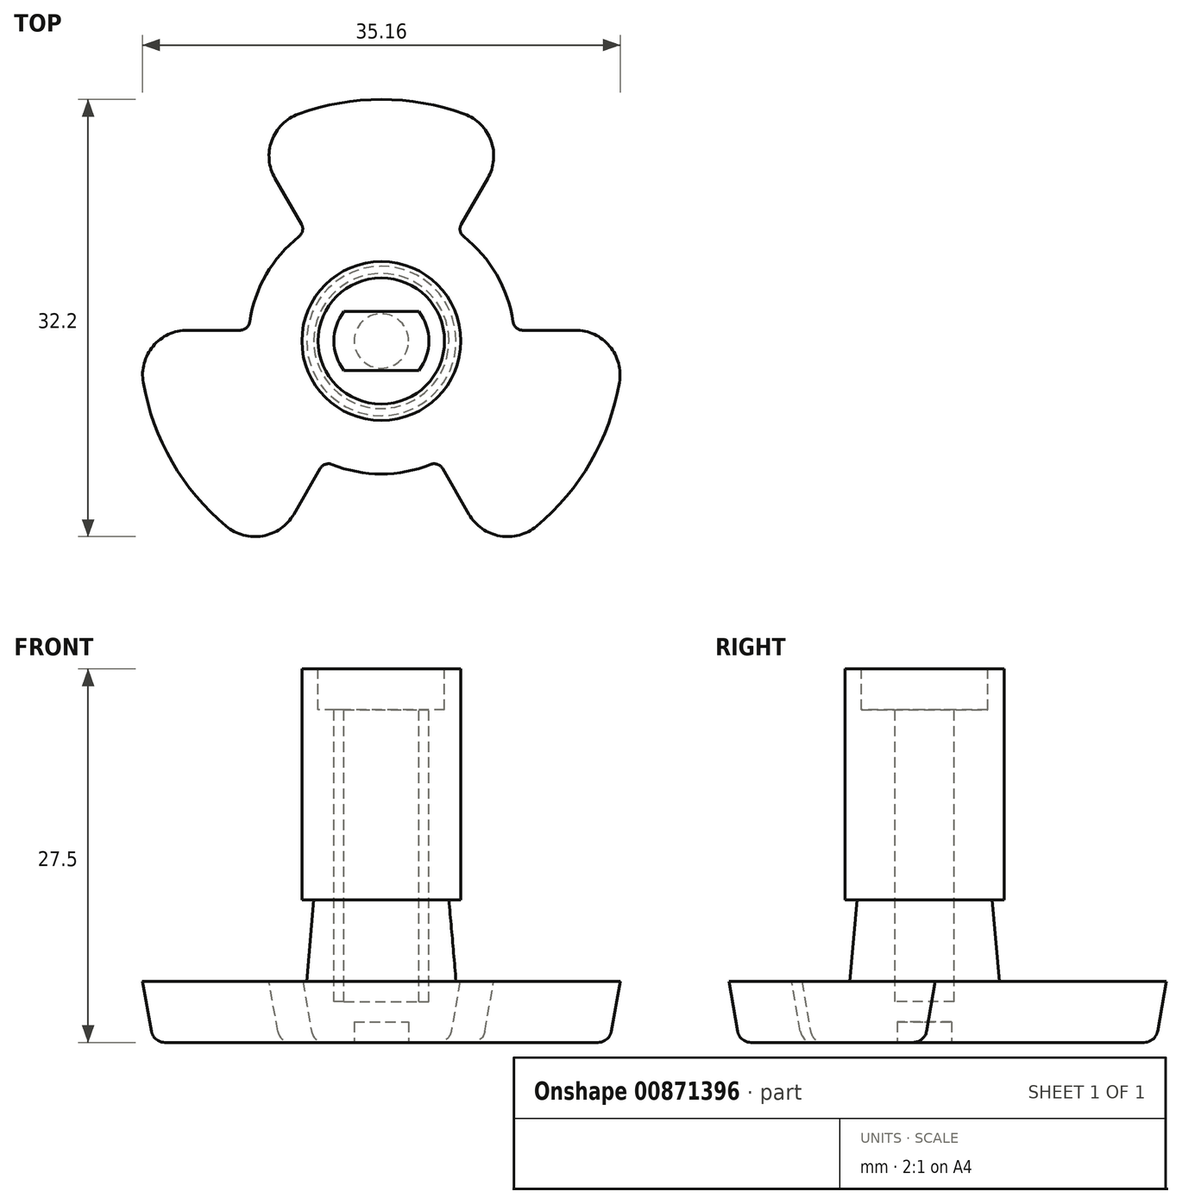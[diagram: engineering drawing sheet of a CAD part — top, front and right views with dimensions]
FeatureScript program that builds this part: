
annotation { "Feature Type Name" : "Feature", "Feature Type Description" : "" }
export const myFeature = defineFeature(function(context is Context, id is Id, definition is map)
    precondition{}
    {
        {
            var Q0;
            Q0=qCreatedBy(makeId("Top.planeOp"),FACE);
            var sketch = newSketch(context, id + "F0", { "sketchPlane" : qUnion([Q0])});
            skArc(sketch, "E0", {"start": v(-16.75, -2.93) * mm, "mid": v(-14.72, -8.5) * mm, "end": v(-10.91, -13.04) * mm});
            skLineSegment(sketch, "E1", {"start": v(-14.28, 0) * mm, "end": v(-10.4, 0) * mm});
            skLineSegment(sketch, "E2.1.0", {"start": v(7.14, -12.37) * mm, "end": v(5.2, -9) * mm});
            skLineSegment(sketch, "E2.2.0", {"start": v(7.14, 12.37) * mm, "end": v(5.2, 9) * mm});
            skArc(sketch, "E3", {"start": v(-5.57, 7.07) * mm, "mid": v(-7.8, 4.5) * mm, "end": v(-8.9, 1.29) * mm});
            skPoint(sketch, "E4.orphan", {"position": v(-10.5, 18.2) * mm});
            skPoint(sketch, "E5.orphan", {"position": v(10.95, 18.97) * mm});
            skArc(sketch, "E6.trimOffspring", {"start": v(5.83, 15.97) * mm, "mid": v(0, 17) * mm, "end": v(-5.83, 15.97) * mm});
            skPoint(sketch, "E7.orphan", {"position": v(21.02, 0) * mm});
            skArc(sketch, "E8.trimOffspring", {"start": v(10.91, -13.04) * mm, "mid": v(14.72, -8.5) * mm, "end": v(16.75, -2.93) * mm});
            skPoint(sketch, "E9.orphan", {"position": v(10.95, -18.97) * mm});
            skPoint(sketch, "E10.orphan", {"position": v(-10.5, -18.2) * mm});
            skPoint(sketch, "E11.visualSharp", {"position": v(-8.5, 14.72) * mm});
            skArc(sketch, "E11.filletArc", {"start": v(-5.83, 15.97) * mm, "mid": v(-7.33, 14.47) * mm, "end": v(-7.14, 12.37) * mm});
            skPoint(sketch, "E12.visualSharp", {"position": v(8.5, 14.72) * mm});
            skArc(sketch, "E12.filletArc", {"start": v(7.14, 12.37) * mm, "mid": v(7.33, 14.47) * mm, "end": v(5.83, 15.97) * mm});
            skPoint(sketch, "E13.visualSharp", {"position": v(17, 0) * mm});
            skArc(sketch, "E13.filletArc", {"start": v(16.75, -2.93) * mm, "mid": v(16.2, -0.9) * mm, "end": v(14.28, 0) * mm});
            skPoint(sketch, "E14.visualSharp", {"position": v(8.5, -14.72) * mm});
            skArc(sketch, "E14.filletArc", {"start": v(7.14, -12.37) * mm, "mid": v(8.87, -13.58) * mm, "end": v(10.91, -13.04) * mm});
            skPoint(sketch, "E15.visualSharp", {"position": v(-8.5, -14.72) * mm});
            skArc(sketch, "E15.filletArc", {"start": v(-10.91, -13.04) * mm, "mid": v(-8.87, -13.58) * mm, "end": v(-7.14, -12.37) * mm});
            skPoint(sketch, "E16.orphan", {"position": v(-21.9, 0) * mm});
            skPoint(sketch, "E17.visualSharp", {"position": v(-17, 0) * mm});
            skArc(sketch, "E17.filletArc", {"start": v(-14.28, 0) * mm, "mid": v(-16.2, -0.9) * mm, "end": v(-16.75, -2.93) * mm});
            skLineSegment(sketch, "E18.trimOffspring", {"start": v(-5.2, 9) * mm, "end": v(-7.14, 12.37) * mm});
            skLineSegment(sketch, "E19.trimOffspring", {"start": v(10.4, 0) * mm, "end": v(14.28, 0) * mm});
            skArc(sketch, "E20.trimOffspring", {"start": v(-3.34, -8.36) * mm, "mid": v(0, -9) * mm, "end": v(3.34, -8.36) * mm});
            skLineSegment(sketch, "E21.trimOffspring", {"start": v(-5.2, -9) * mm, "end": v(-7.14, -12.37) * mm});
            skArc(sketch, "E22.trimOffspring", {"start": v(8.9, 1.29) * mm, "mid": v(7.8, 4.5) * mm, "end": v(5.57, 7.07) * mm});
            skPoint(sketch, "E23.visualSharp", {"position": v(-4.5, 7.8) * mm});
            skArc(sketch, "E23.filletArc", {"start": v(-5.57, 7.07) * mm, "mid": v(-5.02, 7.97) * mm, "end": v(-5.2, 9) * mm});
            skPoint(sketch, "E24.visualSharp", {"position": v(-9, 0) * mm});
            skArc(sketch, "E24.filletArc", {"start": v(-10.4, 0) * mm, "mid": v(-9.41, 0.37) * mm, "end": v(-8.9, 1.29) * mm});
            skPoint(sketch, "E25.visualSharp", {"position": v(-4.5, -7.8) * mm});
            skArc(sketch, "E25.filletArc", {"start": v(-3.34, -8.36) * mm, "mid": v(-4.39, -8.33) * mm, "end": v(-5.2, -9) * mm});
            skPoint(sketch, "E26.visualSharp", {"position": v(4.5, -7.8) * mm});
            skArc(sketch, "E26.filletArc", {"start": v(5.2, -9) * mm, "mid": v(4.39, -8.33) * mm, "end": v(3.34, -8.36) * mm});
            skPoint(sketch, "E27.visualSharp", {"position": v(9, 0) * mm});
            skArc(sketch, "E27.filletArc", {"start": v(8.9, 1.29) * mm, "mid": v(9.41, 0.37) * mm, "end": v(10.4, 0) * mm});
            skPoint(sketch, "E28.visualSharp", {"position": v(4.5, 7.8) * mm});
            skArc(sketch, "E28.filletArc", {"start": v(5.2, 9) * mm, "mid": v(5.02, 7.97) * mm, "end": v(5.57, 7.07) * mm});
            skSolve(sketch);
        }
        {
            var Q0;
            Q0 = qSketchRegion(id + "F0", true);
            extrude(context, id + "F1", {"entities" : qUnion([Q0]), "depth" : 4.5 * mm, "offsetDistance" : 25 * mm, "hasDraft" : true, "draftAngle" : 10 * degree});
        }
        {
            var Q0;
            Q0=makeQuery(id+"F1.opExtrude","CAP_FACE",FACE,{"disambiguationData":[OSD([sQuery(id+"F0.wireOp",EDGE,"E0"),sQuery(id+"F0.wireOp",EDGE,"E1"),sQuery(id+"F0.wireOp",EDGE,"E2.1.0"),sQuery(id+"F0.wireOp",EDGE,"E2.2.0"),sQuery(id+"F0.wireOp",EDGE,"E3"),sQuery(id+"F0.wireOp",EDGE,"E6.trimOffspring"),sQuery(id+"F0.wireOp",EDGE,"E8.trimOffspring"),sQuery(id+"F0.wireOp",EDGE,"E11.filletArc"),sQuery(id+"F0.wireOp",EDGE,"E12.filletArc"),sQuery(id+"F0.wireOp",EDGE,"E13.filletArc"),sQuery(id+"F0.wireOp",EDGE,"E14.filletArc"),sQuery(id+"F0.wireOp",EDGE,"E15.filletArc"),sQuery(id+"F0.wireOp",EDGE,"E17.filletArc"),sQuery(id+"F0.wireOp",EDGE,"E18.trimOffspring"),sQuery(id+"F0.wireOp",EDGE,"E19.trimOffspring"),sQuery(id+"F0.wireOp",EDGE,"E20.trimOffspring"),sQuery(id+"F0.wireOp",EDGE,"E21.trimOffspring"),sQuery(id+"F0.wireOp",EDGE,"E22.trimOffspring"),sQuery(id+"F0.wireOp",EDGE,"E23.filletArc"),sQuery(id+"F0.wireOp",EDGE,"E24.filletArc"),sQuery(id+"F0.wireOp",EDGE,"E25.filletArc"),sQuery(id+"F0.wireOp",EDGE,"E26.filletArc"),sQuery(id+"F0.wireOp",EDGE,"E27.filletArc"),sQuery(id+"F0.wireOp",EDGE,"E28.filletArc")])],"isStart":false});
            var sketch = newSketch(context, id + "F2", { "sketchPlane" : qUnion([Q0])});
            skCircle(sketch, "E29", {"center": v(0, 0) * mm, "radius": 5.5 * mm});
            skSolve(sketch);
        }
        {
            var Q0;
            Q0 = qSketchRegion(id + "F2", true);
            extrude(context, id + "F3", {"entities" : qUnion([Q0]), "operationType" : NewBodyOperationType.ADD, "depth" : 6 * mm, "offsetDistance" : 25 * mm, "hasDraft" : true, "draftAngle" : 5 * degree, "draftPullDirection" : true});
        }
        {
            var Q0;
            Q0=makeQuery(id+"F3.opExtrude","CAP_FACE",FACE,{"disambiguationData":[OSD([sQuery(id+"F2.wireOp",EDGE,"E29")])],"isStart":false});
            var sketch = newSketch(context, id + "F4", { "sketchPlane" : qUnion([Q0])});
            skCircle(sketch, "E30", {"center": v(0, 0) * mm, "radius": 5.85 * mm});
            skSolve(sketch);
        }
        {
            var Q0;
            Q0 = qSketchRegion(id + "F4", true);
            extrude(context, id + "F5", {"entities" : qUnion([Q0]), "operationType" : NewBodyOperationType.ADD, "depth" : 17 * mm, "offsetDistance" : 25 * mm});
        }
        {
            var Q0;
            Q0=makeQuery(id+"F1.opExtrude","CAP_EDGE",EDGE,{"disambiguationData":[OSD([sQuery(id+"F0.wireOp",EDGE,"E20.trimOffspring")])],"isStart":true});
            var Q1;
            Q1=makeQuery(id+"F3.opExtrude","CAP_EDGE",EDGE,{"disambiguationData":[OSD([sQuery(id+"F2.wireOp",EDGE,"E29")])],"isStart":false});
            fillet(context, id + "F6", {"entities" : qUnion([Q0, Q1]), "radius" : 1 * mm, "tangentPropagation" : true, "allowEdgeOverflow" : false});
        }
        {
            var Q0;
            Q0=makeQuery(id+"F5.opExtrude","CAP_FACE",FACE,{"disambiguationData":[OSD([sQuery(id+"F4.wireOp",EDGE,"E30")])],"isStart":false});
            var sketch = newSketch(context, id + "F7", { "sketchPlane" : qUnion([Q0])});
            skCircle(sketch, "E31", {"center": v(0, 0) * mm, "radius": 4.65 * mm});
            skSolve(sketch);
        }
        {
            var Q0;
            Q0 = qSketchRegion(id + "F7", true);
            extrude(context, id + "F8", {"entities" : qUnion([Q0]), "operationType" : NewBodyOperationType.REMOVE, "oppositeDirection" : true, "depth" : 3 * mm, "offsetDistance" : 25 * mm});
        }
        {
            var Q0;
            Q0=makeQuery(id+"F8.boolean.opBoolean","COPY",FACE,{"derivedFrom":makeQuery(id+"F8.opExtrude","CAP_FACE",FACE,{"disambiguationData":[OSD([sQuery(id+"F7.wireOp",EDGE,"E31")])],"isStart":false})});
            var sketch = newSketch(context, id + "F9", { "sketchPlane" : qUnion([Q0])});
            skArc(sketch, "E32", {"start": v(-2.75, 2.17) * mm, "mid": v(-3.5, 0) * mm, "end": v(-2.75, -2.17) * mm});
            skLineSegment(sketch, "E33", {"start": v(-7.7, 0) * mm, "end": v(8.56, 0) * mm, "construction": true});
            skLineSegment(sketch, "E34", {"start": v(-2.75, 2.17) * mm, "end": v(2.75, 2.17) * mm});
            skLineSegment(sketch, "E35", {"start": v(-2.75, -2.17) * mm, "end": v(2.75, -2.17) * mm});
            skArc(sketch, "E36.trimOffspring", {"start": v(2.75, -2.17) * mm, "mid": v(3.5, 0) * mm, "end": v(2.75, 2.17) * mm});
            skSolve(sketch);
        }
        {
            var Q0;
            Q0 = qSketchRegion(id + "F9", true);
            extrude(context, id + "F10", {"entities" : qUnion([Q0]), "operationType" : NewBodyOperationType.REMOVE, "oppositeDirection" : true, "depth" : 21.5 * mm, "offsetDistance" : 25 * mm});
        }
        {
            var Q0;
            Q0=makeQuery(id+"F1.opExtrude","CAP_FACE",FACE,{"disambiguationData":[OSD([sQuery(id+"F0.wireOp",EDGE,"E0"),sQuery(id+"F0.wireOp",EDGE,"E1"),sQuery(id+"F0.wireOp",EDGE,"E2.1.0"),sQuery(id+"F0.wireOp",EDGE,"E2.2.0"),sQuery(id+"F0.wireOp",EDGE,"E3"),sQuery(id+"F0.wireOp",EDGE,"E6.trimOffspring"),sQuery(id+"F0.wireOp",EDGE,"E8.trimOffspring"),sQuery(id+"F0.wireOp",EDGE,"E11.filletArc"),sQuery(id+"F0.wireOp",EDGE,"E12.filletArc"),sQuery(id+"F0.wireOp",EDGE,"E13.filletArc"),sQuery(id+"F0.wireOp",EDGE,"E14.filletArc"),sQuery(id+"F0.wireOp",EDGE,"E15.filletArc"),sQuery(id+"F0.wireOp",EDGE,"E17.filletArc"),sQuery(id+"F0.wireOp",EDGE,"E18.trimOffspring"),sQuery(id+"F0.wireOp",EDGE,"E19.trimOffspring"),sQuery(id+"F0.wireOp",EDGE,"E20.trimOffspring"),sQuery(id+"F0.wireOp",EDGE,"E21.trimOffspring"),sQuery(id+"F0.wireOp",EDGE,"E22.trimOffspring"),sQuery(id+"F0.wireOp",EDGE,"E23.filletArc"),sQuery(id+"F0.wireOp",EDGE,"E24.filletArc"),sQuery(id+"F0.wireOp",EDGE,"E25.filletArc"),sQuery(id+"F0.wireOp",EDGE,"E26.filletArc"),sQuery(id+"F0.wireOp",EDGE,"E27.filletArc"),sQuery(id+"F0.wireOp",EDGE,"E28.filletArc")])],"isStart":true});
            var sketch = newSketch(context, id + "F11", { "sketchPlane" : qUnion([Q0])});
            skCircle(sketch, "E37", {"center": v(0, 0) * mm, "radius": 2 * mm});
            skSolve(sketch);
        }
        {
            var Q0;
            Q0 = qSketchRegion(id + "F11", true);
            extrude(context, id + "F12", {"entities" : qUnion([Q0]), "operationType" : NewBodyOperationType.REMOVE, "oppositeDirection" : true, "depth" : 1.5 * mm, "offsetDistance" : 25 * mm});
        }
    });
